# Revit family: Окна раздвижные RI 40 BG двухстворчатые с глухой частью
name_source: partatom
category: Окна
revit_build: Autodesk Revit 2016 (Build: 20160314_0715(x64)
units: mm (PartAtom-declared; Revit-internal decimal feet)

## family parameters
Всегда вертикально = Да
Заголовок OmniClass = Windows
Номер OmniClass = 23.30.20.00
Общий = Нет
Основа = Стена
При загрузке вырезать с полостями = Нет
Точка расчета площади = Нет

## types (1)
- Окна раздвижные RI 40 BG трёхстворчатые с глухой частью
    ADSK_Версия Revit = Revit 2016
    ADSK_Единица измерения = шт.
    ADSK_Наименование краткое = Окна раздвижные RI 40 BG
    Rед = 1.0000 (м²·K)/Вт
    Rпрофиля = 1.0000 (м²·K)/Вт
    Rстеклопакета = 1.0000 (м²·K)/Вт
    URL = http://www.realit.ru
    λ краевой зоны стеклопакета = 0.0000 (м²·K)/Вт
    Аналитическая конструкция = <Нет>
    Высота = 0 мм
    Замыкание стены = По основе
    Изготовитель = REALIT
    Материал-Монтажный зазор = REALIT_Монтажный шов
    Материал-Подоконник = REALIT_ПВХ_Белый
    Материал-Рама = REALIT_Профиль_RAL 9016
    Материал-Стеклопакет = REALIT_Стекло
    Наименование = Окна раздвижные RI 40 BG трёхстворчатые с глухой частью
    Примерная высота = 0 мм
    Примерная ширина = 0 мм
    Стеклопакет.Толщина = 6 мм
    Толщина = 0 мм
    Толщина стеклопакета = 6
    Цвет профиля = RAL 9016
    Ширина = 0 мм

## geometry (parser evidence)
native form markers: Blend x2
no freeform markers — native parametric forms only
